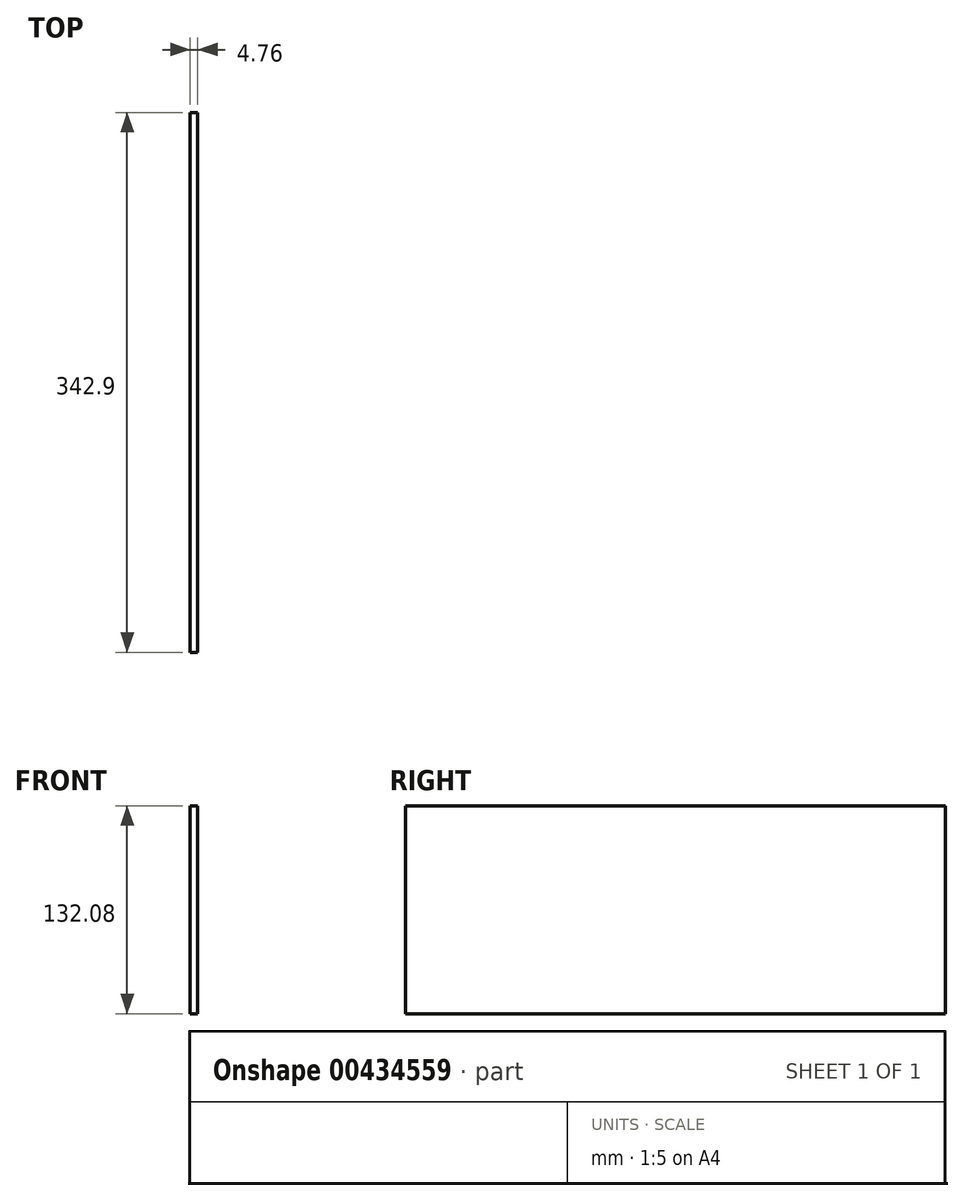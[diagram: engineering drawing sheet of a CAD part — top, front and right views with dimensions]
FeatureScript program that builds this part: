
annotation { "Feature Type Name" : "Feature", "Feature Type Description" : "" }
export const myFeature = defineFeature(function(context is Context, id is Id, definition is map)
    precondition{}
    {
        {
            var Q0;
            Q0=qCreatedBy(makeId("Right.planeOp"),FACE);
            var sketch = newSketch(context, id + "F0", { "sketchPlane" : qUnion([Q0])});
            skLineSegment(sketch, "E0.bottom", {"start": v(-80.9, 71.66) * mm, "end": v(262, 71.66) * mm});
            skLineSegment(sketch, "E0.top", {"start": v(-80.9, -60.42) * mm, "end": v(262, -60.42) * mm});
            skLineSegment(sketch, "E0.left", {"start": v(-80.9, 71.66) * mm, "end": v(-80.9, -60.42) * mm});
            skLineSegment(sketch, "E0.right", {"start": v(262, 71.66) * mm, "end": v(262, -60.42) * mm});
            skSolve(sketch);
        }
        {
            var Q0;
            Q0=makeQuery(id+"F0.imprint","IMPRINT",FACE,{"disambiguationData":[TD([[makeQuery(id+"F0.imprint","IMPRINT",EDGE,{"derivedFrom":sQuery(id+"F0.wireOp",EDGE,"E0.bottom")}),-1.0]])]});
            extrude(context, id + "F1", {"entities" : qUnion([Q0]), "depth" : 4.76 * mm});
        }
    });
